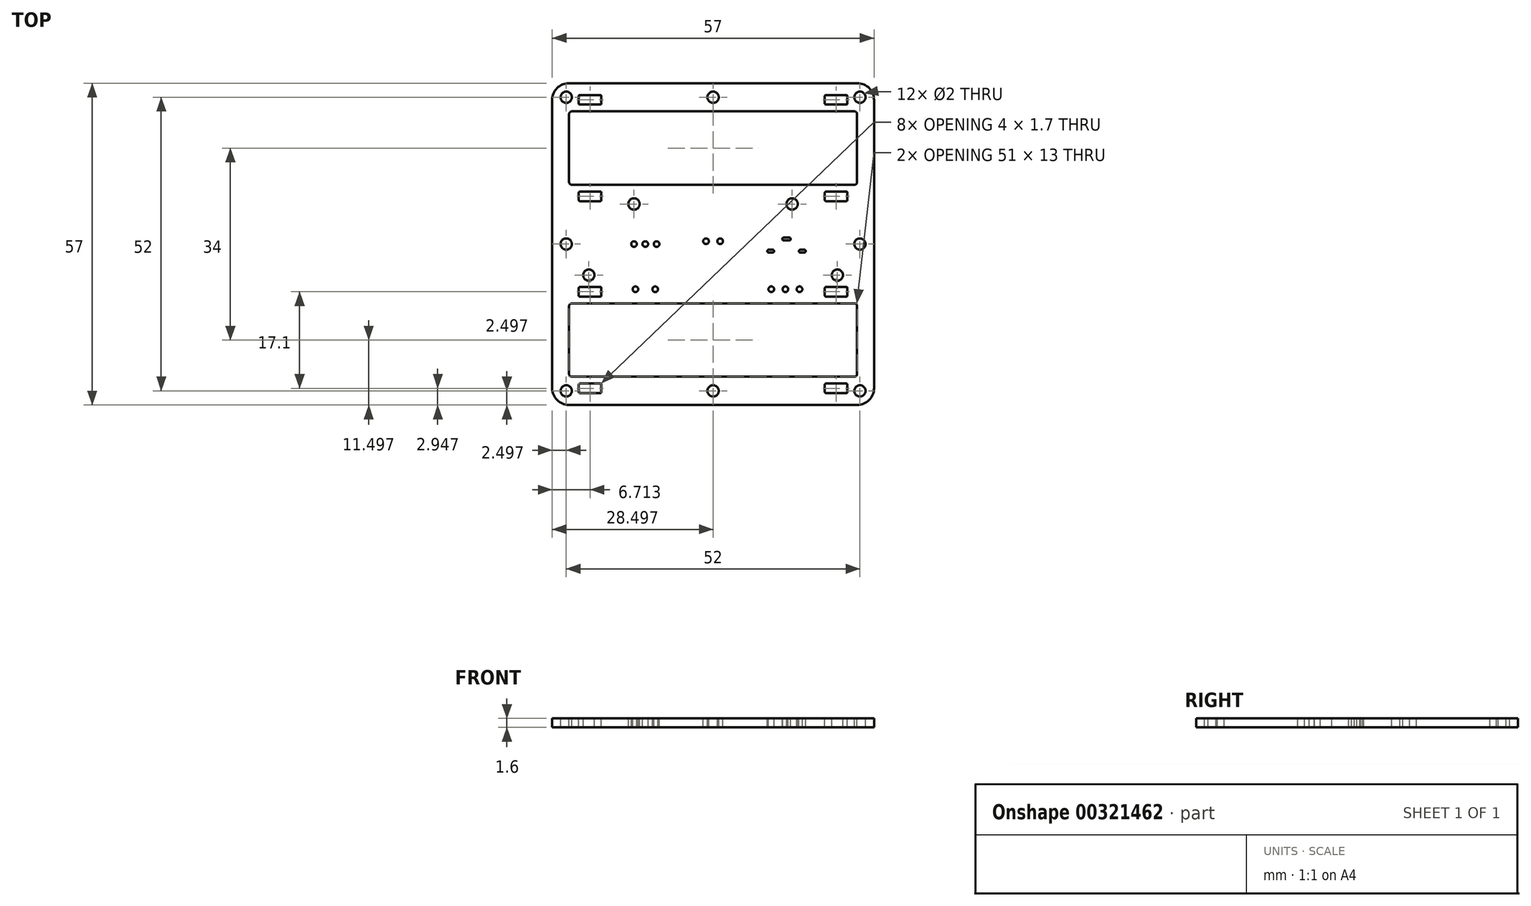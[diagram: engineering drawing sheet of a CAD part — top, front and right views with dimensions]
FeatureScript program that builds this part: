
annotation { "Feature Type Name" : "Feature", "Feature Type Description" : "" }
export const myFeature = defineFeature(function(context is Context, id is Id, definition is map)
    precondition{}
    {
        {
            var Q0;
            Q0=qCreatedBy(makeId("Top.planeOp"),FACE);
            var sketch = newSketch(context, id + "F0", { "sketchPlane" : qUnion([Q0])});
            skLineSegment(sketch, "E0.bottom", {"start": v(24.47, 58.7) * mm, "end": v(66.84, 58.7) * mm, "construction": true});
            skLineSegment(sketch, "E1.bottom", {"start": v(12.82, 58.7) * mm, "end": v(69.82, 58.7) * mm});
            skLineSegment(sketch, "E1.top", {"start": v(12.82, 1.7) * mm, "end": v(69.82, 1.7) * mm});
            skLineSegment(sketch, "E1.left", {"start": v(12.82, 58.7) * mm, "end": v(12.82, 1.7) * mm});
            skLineSegment(sketch, "E1.right", {"start": v(69.82, 58.7) * mm, "end": v(69.82, 1.7) * mm});
            skLineSegment(sketch, "E2", {"start": v(41.32, 58.7) * mm, "end": v(41.32, 1.7) * mm, "construction": true});
            skSolve(sketch);
        }
        {
            var Q0;
            Q0=qSketchRegion(id+"F0",true);
            extrude(context, id + "F1", {"entities" : qUnion([Q0]), "depth" : 1.6 * mm});
        }
        {
            var Q0;
            Q0=makeQuery(id+"F1.opExtrude","CAP_FACE",FACE,{"disambiguationData":[OSD([sQuery(id+"F0.wireOp",EDGE,"E1.bottom"),sQuery(id+"F0.wireOp",EDGE,"E1.top"),sQuery(id+"F0.wireOp",EDGE,"E1.left"),sQuery(id+"F0.wireOp",EDGE,"E1.right")])],"isStart":false});
            var sketch = newSketch(context, id + "F2", { "sketchPlane" : qUnion([Q0])});
            skCircle(sketch, "E3", {"center": v(27.32, 30.2) * mm, "radius": 0.5 * mm});
            skLineSegment(sketch, "E4", {"start": v(41.32, 22.32) * mm, "end": v(41.32, 29.29) * mm, "construction": true});
            skCircle(sketch, "E5.1.0.0", {"center": v(29.32, 30.2) * mm, "radius": 0.5 * mm});
            skLineSegment(sketch, "E5.direction1", {"start": v(27.32, 30.2) * mm, "end": v(29.32, 30.2) * mm, "construction": true});
            skCircle(sketch, "E6.0.2.0", {"center": v(31.32, 30.2) * mm, "radius": 0.5 * mm});
            skSolve(sketch);
        }
        {
            var Q0;
            Q0=makeQuery(id+"F1.opExtrude","CAP_FACE",FACE,{"disambiguationData":[OSD([sQuery(id+"F0.wireOp",EDGE,"E1.bottom"),sQuery(id+"F0.wireOp",EDGE,"E1.top"),sQuery(id+"F0.wireOp",EDGE,"E1.left"),sQuery(id+"F0.wireOp",EDGE,"E1.right")])],"isStart":false});
            var sketch = newSketch(context, id + "F3", { "sketchPlane" : qUnion([Q0])});
            skLineSegment(sketch, "E7", {"start": v(54.32, 14.1) * mm, "end": v(54.32, 27.42) * mm, "construction": true});
            skLineSegment(sketch, "E8", {"start": v(41.32, 6.29) * mm, "end": v(41.32, 24.04) * mm, "construction": true});
            skLineSegment(sketch, "E9", {"start": v(51.17, 28.95) * mm, "end": v(51.87, 28.95) * mm, "construction": true});
            skLineSegment(sketch, "E10", {"start": v(51.52, 23.97) * mm, "end": v(51.52, 28.95) * mm, "construction": true});
            skLineSegment(sketch, "E11", {"start": v(53.82, 31.1) * mm, "end": v(54.82, 31.1) * mm, "construction": true});
            skLineSegment(sketch, "E12", {"start": v(54.32, 31.1) * mm, "end": v(54.32, 19.92) * mm, "construction": true});
            skArc(sketch, "E13.0.startCap", {"start": v(53.82, 30.85) * mm, "mid": v(53.57, 31.1) * mm, "end": v(53.82, 31.35) * mm});
            skArc(sketch, "E13.0.endCap", {"start": v(54.82, 31.35) * mm, "mid": v(55.07, 31.1) * mm, "end": v(54.82, 30.85) * mm});
            skLineSegment(sketch, "E13.0.left", {"start": v(53.82, 31.35) * mm, "end": v(54.82, 31.35) * mm});
            skLineSegment(sketch, "E13.0.right", {"start": v(53.82, 30.85) * mm, "end": v(54.82, 30.85) * mm});
            skLineSegment(sketch, "E14", {"start": v(50.45, 30.1) * mm, "end": v(53.65, 30.1) * mm, "construction": true});
            skArc(sketch, "E15.0.startCap", {"start": v(51.87, 29.2) * mm, "mid": v(52.12, 28.95) * mm, "end": v(51.87, 28.7) * mm});
            skArc(sketch, "E15.0.endCap", {"start": v(51.17, 28.7) * mm, "mid": v(50.92, 28.95) * mm, "end": v(51.17, 29.2) * mm});
            skLineSegment(sketch, "E15.0.left", {"start": v(51.17, 28.7) * mm, "end": v(51.87, 28.7) * mm});
            skLineSegment(sketch, "E15.0.right", {"start": v(51.17, 29.2) * mm, "end": v(51.87, 29.2) * mm});
            skArc(sketch, "E16.MirrorCS", {"start": v(57.47, 28.7) * mm, "mid": v(57.72, 28.95) * mm, "end": v(57.47, 29.2) * mm});
            skLineSegment(sketch, "E17.MirrorCS", {"start": v(57.47, 28.7) * mm, "end": v(56.77, 28.7) * mm});
            skLineSegment(sketch, "E18.MirrorCS", {"start": v(57.47, 29.2) * mm, "end": v(56.77, 29.2) * mm});
            skArc(sketch, "E19.MirrorCS", {"start": v(56.77, 29.2) * mm, "mid": v(56.52, 28.95) * mm, "end": v(56.77, 28.7) * mm});
            skSolve(sketch);
        }
        {
            var Q0;
            Q0=makeQuery(id+"F1.opExtrude","CAP_FACE",FACE,{"disambiguationData":[OSD([sQuery(id+"F0.wireOp",EDGE,"E1.bottom"),sQuery(id+"F0.wireOp",EDGE,"E1.top"),sQuery(id+"F0.wireOp",EDGE,"E1.left"),sQuery(id+"F0.wireOp",EDGE,"E1.right")])],"isStart":false});
            var sketch = newSketch(context, id + "F4", { "sketchPlane" : qUnion([Q0])});
            skCircle(sketch, "E20", {"center": v(51.62, 22.2) * mm, "radius": 0.5 * mm});
            skCircle(sketch, "E21.1.0.0", {"center": v(56.62, 22.2) * mm, "radius": 0.5 * mm});
            skLineSegment(sketch, "E21.direction1", {"start": v(51.62, 22.2) * mm, "end": v(56.62, 22.2) * mm, "construction": true});
            skLineSegment(sketch, "E22", {"start": v(41.32, 6.29) * mm, "end": v(41.32, 17.65) * mm, "construction": true});
            skLineSegment(sketch, "E23", {"start": v(54.12, 22.2) * mm, "end": v(54.12, 23.7) * mm, "construction": true});
            skCircle(sketch, "E24", {"center": v(54.12, 22.2) * mm, "radius": 0.5 * mm});
            skSolve(sketch);
        }
        {
            var Q0;
            Q0=makeQuery(id+"F1.opExtrude","CAP_FACE",FACE,{"disambiguationData":[OSD([sQuery(id+"F0.wireOp",EDGE,"E1.bottom"),sQuery(id+"F0.wireOp",EDGE,"E1.top"),sQuery(id+"F0.wireOp",EDGE,"E1.left"),sQuery(id+"F0.wireOp",EDGE,"E1.right")])],"isStart":false});
            var sketch = newSketch(context, id + "F5", { "sketchPlane" : qUnion([Q0])});
            skCircle(sketch, "E25", {"center": v(40.07, 30.7) * mm, "radius": 0.5 * mm});
            skCircle(sketch, "E26.1.0.0", {"center": v(42.57, 30.7) * mm, "radius": 0.5 * mm});
            skLineSegment(sketch, "E26.direction1", {"start": v(40.07, 30.7) * mm, "end": v(42.57, 30.7) * mm, "construction": true});
            skLineSegment(sketch, "E27", {"start": v(41.32, 15.29) * mm, "end": v(41.32, 29.29) * mm, "construction": true});
            skLineSegment(sketch, "E28", {"start": v(41.32, 26.14) * mm, "end": v(41.32, 30.7) * mm, "construction": true});
            skSolve(sketch);
        }
        {
            var Q0;
            Q0=makeQuery(id+"F1.opExtrude","CAP_FACE",FACE,{"disambiguationData":[OSD([sQuery(id+"F0.wireOp",EDGE,"E1.bottom"),sQuery(id+"F0.wireOp",EDGE,"E1.top"),sQuery(id+"F0.wireOp",EDGE,"E1.left"),sQuery(id+"F0.wireOp",EDGE,"E1.right")])],"isStart":false});
            var sketch = newSketch(context, id + "F6", { "sketchPlane" : qUnion([Q0])});
            skCircle(sketch, "E29", {"center": v(27.57, 22.2) * mm, "radius": 0.5 * mm});
            skCircle(sketch, "E30.1.0.0", {"center": v(31.07, 22.2) * mm, "radius": 0.5 * mm});
            skLineSegment(sketch, "E30.direction1", {"start": v(27.57, 22.2) * mm, "end": v(31.07, 22.2) * mm, "construction": true});
            skLineSegment(sketch, "E31", {"start": v(29.32, 26.4) * mm, "end": v(29.32, 22.2) * mm, "construction": true});
            skSolve(sketch);
        }
        {
            var Q0;
            Q0=qSketchRegion(id+"F4",true);
            var Q1;
            Q1=qSketchRegion(id+"F5",true);
            var Q2;
            Q2=qSketchRegion(id+"F6",true);
            var Q3;
            Q3=qSketchRegion(id+"F3",true);
            var Q4;
            Q4=qSketchRegion(id+"F2",true);
            extrude(context, id + "F7", {"entities" : qUnion([Q0, Q1, Q2, Q3, Q4]), "operationType" : NewBodyOperationType.REMOVE, "oppositeDirection" : true, "depth" : 4 * mm});
        }
        {
            var Q0;
            Q0=makeQuery(id+"F1.opExtrude","SWEPT_EDGE",EDGE,{"disambiguationData":[OSD([sQuery(id+"F0.wireOp",EDGE,"E1.top"),sQuery(id+"F0.wireOp",EDGE,"E1.left")])]});
            var Q1;
            Q1=makeQuery(id+"F1.opExtrude","SWEPT_EDGE",EDGE,{"disambiguationData":[OSD([sQuery(id+"F0.wireOp",EDGE,"E1.top"),sQuery(id+"F0.wireOp",EDGE,"E1.right")])]});
            var Q2;
            Q2=makeQuery(id+"F1.opExtrude","SWEPT_EDGE",EDGE,{"disambiguationData":[OSD([sQuery(id+"F0.wireOp",EDGE,"E1.bottom"),sQuery(id+"F0.wireOp",EDGE,"E1.right")])]});
            var Q3;
            Q3=makeQuery(id+"F1.opExtrude","SWEPT_EDGE",EDGE,{"disambiguationData":[OSD([sQuery(id+"F0.wireOp",EDGE,"E1.bottom"),sQuery(id+"F0.wireOp",EDGE,"E1.left")])]});
            fillet(context, id + "F8", {"entities" : qUnion([Q0, Q1, Q2, Q3]), "radius" : 3 * mm, "tangentPropagation" : true, "allowEdgeOverflow" : false});
        }
        {
            var Q0;
            Q0=makeQuery(id+"F1.opExtrude","CAP_FACE",FACE,{"disambiguationData":[OSD([sQuery(id+"F0.wireOp",EDGE,"E1.bottom"),sQuery(id+"F0.wireOp",EDGE,"E1.top"),sQuery(id+"F0.wireOp",EDGE,"E1.left"),sQuery(id+"F0.wireOp",EDGE,"E1.right")])],"isStart":false});
            var sketch = newSketch(context, id + "F9", { "sketchPlane" : qUnion([Q0])});
            skLineSegment(sketch, "E32", {"start": v(41.32, 58.7) * mm, "end": v(41.32, 1.7) * mm, "construction": true});
            skLineSegment(sketch, "E33", {"start": v(12.82, 30.2) * mm, "end": v(69.82, 30.2) * mm, "construction": true});
            skCircle(sketch, "E34", {"center": v(63.32, 24.7) * mm, "radius": 1 * mm});
            skCircle(sketch, "E35.MirrorC", {"center": v(19.32, 24.7) * mm, "radius": 1 * mm});
            skCircle(sketch, "E36", {"center": v(55.32, 37.3) * mm, "radius": 1 * mm});
            skCircle(sketch, "E37.MirrorC", {"center": v(27.32, 37.3) * mm, "radius": 1 * mm});
            skCircle(sketch, "E38", {"center": v(15.32, 56.2) * mm, "radius": 1 * mm});
            skCircle(sketch, "E39.MirrorC", {"center": v(67.32, 56.2) * mm, "radius": 1 * mm});
            skCircle(sketch, "E40.MirrorC", {"center": v(15.32, 4.2) * mm, "radius": 1 * mm});
            skCircle(sketch, "E41.MirrorC", {"center": v(67.32, 4.2) * mm, "radius": 1 * mm});
            skCircle(sketch, "E42", {"center": v(41.32, 56.2) * mm, "radius": 1 * mm});
            skCircle(sketch, "E43.MirrorC", {"center": v(41.32, 4.2) * mm, "radius": 1 * mm});
            skCircle(sketch, "E44", {"center": v(15.32, 30.2) * mm, "radius": 1 * mm});
            skCircle(sketch, "E45", {"center": v(67.32, 30.2) * mm, "radius": 1 * mm});
            skSolve(sketch);
        }
        {
            var Q0;
            Q0=qSketchRegion(id+"F9",true);
            extrude(context, id + "F10", {"entities" : qUnion([Q0]), "operationType" : NewBodyOperationType.REMOVE, "oppositeDirection" : true, "depth" : 25 * mm});
        }
        {
            var Q0;
            Q0=makeQuery(id+"F1.opExtrude","CAP_FACE",FACE,{"disambiguationData":[OSD([sQuery(id+"F0.wireOp",EDGE,"E1.bottom"),sQuery(id+"F0.wireOp",EDGE,"E1.top"),sQuery(id+"F0.wireOp",EDGE,"E1.left"),sQuery(id+"F0.wireOp",EDGE,"E1.right")])],"isStart":false});
            var sketch = newSketch(context, id + "F11", { "sketchPlane" : qUnion([Q0])});
            skLineSegment(sketch, "E46", {"start": v(41.32, 58.7) * mm, "end": v(41.32, 1.7) * mm, "construction": true});
            skLineSegment(sketch, "E47.bottom", {"start": v(66.32, 19.7) * mm, "end": v(16.32, 19.7) * mm});
            skLineSegment(sketch, "E47.top", {"start": v(66.32, 6.7) * mm, "end": v(16.32, 6.7) * mm});
            skLineSegment(sketch, "E47.left", {"start": v(66.82, 19.2) * mm, "end": v(66.82, 7.2) * mm});
            skLineSegment(sketch, "E47.right", {"start": v(15.82, 19.2) * mm, "end": v(15.82, 7.2) * mm});
            skPoint(sketch, "E47.middle", {"position": v(41.32, 13.2) * mm});
            skLineSegment(sketch, "E48", {"start": v(41.32, 30.2) * mm, "end": v(-6.1, 30.2) * mm, "construction": true});
            skPoint(sketch, "E49.visualSharp", {"position": v(15.82, 6.7) * mm});
            skArc(sketch, "E49.filletArc", {"start": v(15.82, 7.2) * mm, "mid": v(15.96, 6.84) * mm, "end": v(16.32, 6.7) * mm});
            skPoint(sketch, "E50.visualSharp", {"position": v(15.82, 19.7) * mm});
            skArc(sketch, "E50.filletArc", {"start": v(16.32, 19.7) * mm, "mid": v(15.96, 19.55) * mm, "end": v(15.82, 19.2) * mm});
            skPoint(sketch, "E51.visualSharp", {"position": v(66.82, 19.7) * mm});
            skArc(sketch, "E51.filletArc", {"start": v(66.82, 19.2) * mm, "mid": v(66.67, 19.55) * mm, "end": v(66.32, 19.7) * mm});
            skPoint(sketch, "E52.visualSharp", {"position": v(66.82, 6.7) * mm});
            skArc(sketch, "E52.filletArc", {"start": v(66.32, 6.7) * mm, "mid": v(66.67, 6.84) * mm, "end": v(66.82, 7.2) * mm});
            skArc(sketch, "E53.MirrorCS", {"start": v(15.82, 53.2) * mm, "mid": v(15.96, 53.55) * mm, "end": v(16.32, 53.7) * mm});
            skArc(sketch, "E54.MirrorCS", {"start": v(16.32, 40.7) * mm, "mid": v(15.96, 40.84) * mm, "end": v(15.82, 41.2) * mm});
            skArc(sketch, "E55.MirrorCS", {"start": v(66.82, 41.2) * mm, "mid": v(66.67, 40.84) * mm, "end": v(66.32, 40.7) * mm});
            skArc(sketch, "E56.MirrorCS", {"start": v(66.32, 53.7) * mm, "mid": v(66.67, 53.55) * mm, "end": v(66.82, 53.2) * mm});
            skLineSegment(sketch, "E57.MirrorCS", {"start": v(15.82, 41.2) * mm, "end": v(15.82, 53.2) * mm});
            skLineSegment(sketch, "E58.MirrorCS", {"start": v(66.32, 40.7) * mm, "end": v(16.32, 40.7) * mm});
            skLineSegment(sketch, "E59.MirrorCS", {"start": v(66.82, 41.2) * mm, "end": v(66.82, 53.2) * mm});
            skLineSegment(sketch, "E60.MirrorCS", {"start": v(66.32, 53.7) * mm, "end": v(16.32, 53.7) * mm});
            skPoint(sketch, "E61.MirrorP", {"position": v(66.82, 53.7) * mm});
            skPoint(sketch, "E62.MirrorP", {"position": v(15.82, 53.7) * mm});
            skPoint(sketch, "E63.MirrorP", {"position": v(41.32, 47.2) * mm});
            skPoint(sketch, "E64.MirrorP", {"position": v(66.82, 40.7) * mm});
            skPoint(sketch, "E65.MirrorP", {"position": v(15.82, 40.7) * mm});
            skSolve(sketch);
        }
        {
            var Q0;
            Q0=qSketchRegion(id+"F11",true);
            extrude(context, id + "F12", {"entities" : qUnion([Q0]), "operationType" : NewBodyOperationType.REMOVE, "oppositeDirection" : true, "depth" : 5 * mm});
        }
        {
            var Q0;
            Q0=makeQuery(id+"F1.opExtrude","CAP_FACE",FACE,{"disambiguationData":[OSD([sQuery(id+"F0.wireOp",EDGE,"E1.bottom"),sQuery(id+"F0.wireOp",EDGE,"E1.top"),sQuery(id+"F0.wireOp",EDGE,"E1.left"),sQuery(id+"F0.wireOp",EDGE,"E1.right")])],"isStart":false});
            var sketch = newSketch(context, id + "F13", { "sketchPlane" : qUnion([Q0])});
            skLineSegment(sketch, "E66.bottom", {"start": v(17.53, 5.5) * mm, "end": v(21.53, 5.5) * mm});
            skLineSegment(sketch, "E66.top", {"start": v(17.53, 3.8) * mm, "end": v(21.53, 3.8) * mm});
            skLineSegment(sketch, "E66.left", {"start": v(17.53, 5.5) * mm, "end": v(17.53, 3.8) * mm});
            skLineSegment(sketch, "E66.right", {"start": v(21.53, 5.5) * mm, "end": v(21.53, 3.8) * mm});
            skLineSegment(sketch, "E67.MirrorCS", {"start": v(65.1, 5.5) * mm, "end": v(65.1, 3.8) * mm});
            skLineSegment(sketch, "E68.MirrorCS", {"start": v(61.1, 5.5) * mm, "end": v(61.1, 3.8) * mm});
            skLineSegment(sketch, "E69.MirrorCS", {"start": v(65.1, 3.8) * mm, "end": v(61.1, 3.8) * mm});
            skLineSegment(sketch, "E70.MirrorCS", {"start": v(65.1, 5.5) * mm, "end": v(61.1, 5.5) * mm});
            skLineSegment(sketch, "E71", {"start": v(12.82, 30.2) * mm, "end": v(83.5, 30.2) * mm, "construction": true});
            skLineSegment(sketch, "E72", {"start": v(15.82, 13.2) * mm, "end": v(-2.11, 13.2) * mm, "construction": true});
            skPoint(sketch, "E72.endSnap0", {"position": v(15.82, 13.2) * mm});
            skLineSegment(sketch, "E73.MirrorCS", {"start": v(61.1, 20.9) * mm, "end": v(61.1, 22.6) * mm});
            skLineSegment(sketch, "E74.MirrorCS", {"start": v(65.1, 20.9) * mm, "end": v(65.1, 22.6) * mm});
            skLineSegment(sketch, "E75.MirrorCS", {"start": v(21.53, 20.9) * mm, "end": v(21.53, 22.6) * mm});
            skLineSegment(sketch, "E76.MirrorCS", {"start": v(17.53, 20.9) * mm, "end": v(17.53, 22.6) * mm});
            skLineSegment(sketch, "E77.MirrorCS", {"start": v(65.1, 20.9) * mm, "end": v(61.1, 20.9) * mm});
            skLineSegment(sketch, "E78.MirrorCS", {"start": v(65.1, 22.6) * mm, "end": v(61.1, 22.6) * mm});
            skLineSegment(sketch, "E79.MirrorCS", {"start": v(17.53, 22.6) * mm, "end": v(21.53, 22.6) * mm});
            skLineSegment(sketch, "E80.MirrorCS", {"start": v(17.53, 20.9) * mm, "end": v(21.53, 20.9) * mm});
            skLineSegment(sketch, "E81.MirrorCS", {"start": v(17.53, 39.5) * mm, "end": v(17.53, 37.8) * mm});
            skLineSegment(sketch, "E82.MirrorCS", {"start": v(17.53, 54.9) * mm, "end": v(17.53, 56.6) * mm});
            skLineSegment(sketch, "E83.MirrorCS", {"start": v(61.1, 39.5) * mm, "end": v(61.1, 37.8) * mm});
            skLineSegment(sketch, "E84.MirrorCS", {"start": v(21.53, 54.9) * mm, "end": v(21.53, 56.6) * mm});
            skLineSegment(sketch, "E85.MirrorCS", {"start": v(65.1, 54.9) * mm, "end": v(65.1, 56.6) * mm});
            skLineSegment(sketch, "E86.MirrorCS", {"start": v(21.53, 39.5) * mm, "end": v(21.53, 37.8) * mm});
            skLineSegment(sketch, "E87.MirrorCS", {"start": v(61.1, 54.9) * mm, "end": v(61.1, 56.6) * mm});
            skLineSegment(sketch, "E88.MirrorCS", {"start": v(65.1, 39.5) * mm, "end": v(65.1, 37.8) * mm});
            skLineSegment(sketch, "E89.MirrorCS", {"start": v(17.53, 56.6) * mm, "end": v(21.53, 56.6) * mm});
            skLineSegment(sketch, "E90.MirrorCS", {"start": v(65.1, 39.5) * mm, "end": v(61.1, 39.5) * mm});
            skLineSegment(sketch, "E91.MirrorCS", {"start": v(65.1, 37.8) * mm, "end": v(61.1, 37.8) * mm});
            skLineSegment(sketch, "E92.MirrorCS", {"start": v(17.53, 39.5) * mm, "end": v(21.53, 39.5) * mm});
            skLineSegment(sketch, "E93.MirrorCS", {"start": v(17.53, 54.9) * mm, "end": v(21.53, 54.9) * mm});
            skLineSegment(sketch, "E94.MirrorCS", {"start": v(65.1, 56.6) * mm, "end": v(61.1, 56.6) * mm});
            skPoint(sketch, "E95.MirrorP", {"position": v(15.82, 47.2) * mm});
            skLineSegment(sketch, "E96.MirrorCS", {"start": v(65.1, 54.9) * mm, "end": v(61.1, 54.9) * mm});
            skLineSegment(sketch, "E97.MirrorCS", {"start": v(17.53, 37.8) * mm, "end": v(21.53, 37.8) * mm});
            skSolve(sketch);
        }
        {
            var Q0;
            Q0=qSketchRegion(id+"F13",true);
            extrude(context, id + "F14", {"entities" : qUnion([Q0]), "operationType" : NewBodyOperationType.REMOVE, "oppositeDirection" : true, "depth" : 25 * mm});
        }
        {
            var Q0;
            Q0=makeQuery(id+"F14.boolean.opBoolean","COPY",EDGE,{"derivedFrom":makeQuery(id+"F14.opExtrude","SWEPT_EDGE",EDGE,{"disambiguationData":[OSD([sQuery(id+"F13.wireOp",EDGE,"E82.MirrorCS"),sQuery(id+"F13.wireOp",EDGE,"E89.MirrorCS")])]})});
            var Q1;
            Q1=makeQuery(id+"F14.boolean.opBoolean","COPY",EDGE,{"derivedFrom":makeQuery(id+"F14.opExtrude","SWEPT_EDGE",EDGE,{"disambiguationData":[OSD([sQuery(id+"F13.wireOp",EDGE,"E82.MirrorCS"),sQuery(id+"F13.wireOp",EDGE,"E93.MirrorCS")])]})});
            var Q2;
            Q2=makeQuery(id+"F14.boolean.opBoolean","COPY",EDGE,{"derivedFrom":makeQuery(id+"F14.opExtrude","SWEPT_EDGE",EDGE,{"disambiguationData":[OSD([sQuery(id+"F13.wireOp",EDGE,"E84.MirrorCS"),sQuery(id+"F13.wireOp",EDGE,"E93.MirrorCS")])]})});
            var Q3;
            Q3=makeQuery(id+"F14.boolean.opBoolean","COPY",EDGE,{"derivedFrom":makeQuery(id+"F14.opExtrude","SWEPT_EDGE",EDGE,{"disambiguationData":[OSD([sQuery(id+"F13.wireOp",EDGE,"E84.MirrorCS"),sQuery(id+"F13.wireOp",EDGE,"E89.MirrorCS")])]})});
            var Q4;
            Q4=makeQuery(id+"F14.boolean.opBoolean","COPY",EDGE,{"derivedFrom":makeQuery(id+"F14.opExtrude","SWEPT_EDGE",EDGE,{"disambiguationData":[OSD([sQuery(id+"F13.wireOp",EDGE,"E86.MirrorCS"),sQuery(id+"F13.wireOp",EDGE,"E92.MirrorCS")])]})});
            var Q5;
            Q5=makeQuery(id+"F14.boolean.opBoolean","COPY",EDGE,{"derivedFrom":makeQuery(id+"F14.opExtrude","SWEPT_EDGE",EDGE,{"disambiguationData":[OSD([sQuery(id+"F13.wireOp",EDGE,"E81.MirrorCS"),sQuery(id+"F13.wireOp",EDGE,"E92.MirrorCS")])]})});
            var Q6;
            Q6=makeQuery(id+"F14.boolean.opBoolean","COPY",EDGE,{"derivedFrom":makeQuery(id+"F14.opExtrude","SWEPT_EDGE",EDGE,{"disambiguationData":[OSD([sQuery(id+"F13.wireOp",EDGE,"E81.MirrorCS"),sQuery(id+"F13.wireOp",EDGE,"E97.MirrorCS")])]})});
            var Q7;
            Q7=makeQuery(id+"F14.boolean.opBoolean","COPY",EDGE,{"derivedFrom":makeQuery(id+"F14.opExtrude","SWEPT_EDGE",EDGE,{"disambiguationData":[OSD([sQuery(id+"F13.wireOp",EDGE,"E86.MirrorCS"),sQuery(id+"F13.wireOp",EDGE,"E97.MirrorCS")])]})});
            var Q8;
            Q8=makeQuery(id+"F14.boolean.opBoolean","COPY",EDGE,{"derivedFrom":makeQuery(id+"F14.opExtrude","SWEPT_EDGE",EDGE,{"disambiguationData":[OSD([sQuery(id+"F13.wireOp",EDGE,"E85.MirrorCS"),sQuery(id+"F13.wireOp",EDGE,"E96.MirrorCS")])]})});
            var Q9;
            Q9=makeQuery(id+"F14.boolean.opBoolean","COPY",EDGE,{"derivedFrom":makeQuery(id+"F14.opExtrude","SWEPT_EDGE",EDGE,{"disambiguationData":[OSD([sQuery(id+"F13.wireOp",EDGE,"E85.MirrorCS"),sQuery(id+"F13.wireOp",EDGE,"E94.MirrorCS")])]})});
            var Q10;
            Q10=makeQuery(id+"F14.boolean.opBoolean","COPY",EDGE,{"derivedFrom":makeQuery(id+"F14.opExtrude","SWEPT_EDGE",EDGE,{"disambiguationData":[OSD([sQuery(id+"F13.wireOp",EDGE,"E87.MirrorCS"),sQuery(id+"F13.wireOp",EDGE,"E94.MirrorCS")])]})});
            var Q11;
            Q11=makeQuery(id+"F14.boolean.opBoolean","COPY",EDGE,{"derivedFrom":makeQuery(id+"F14.opExtrude","SWEPT_EDGE",EDGE,{"disambiguationData":[OSD([sQuery(id+"F13.wireOp",EDGE,"E87.MirrorCS"),sQuery(id+"F13.wireOp",EDGE,"E96.MirrorCS")])]})});
            var Q12;
            Q12=makeQuery(id+"F14.boolean.opBoolean","COPY",EDGE,{"derivedFrom":makeQuery(id+"F14.opExtrude","SWEPT_EDGE",EDGE,{"disambiguationData":[OSD([sQuery(id+"F13.wireOp",EDGE,"E83.MirrorCS"),sQuery(id+"F13.wireOp",EDGE,"E91.MirrorCS")])]})});
            var Q13;
            Q13=makeQuery(id+"F14.boolean.opBoolean","COPY",EDGE,{"derivedFrom":makeQuery(id+"F14.opExtrude","SWEPT_EDGE",EDGE,{"disambiguationData":[OSD([sQuery(id+"F13.wireOp",EDGE,"E83.MirrorCS"),sQuery(id+"F13.wireOp",EDGE,"E90.MirrorCS")])]})});
            var Q14;
            Q14=makeQuery(id+"F14.boolean.opBoolean","COPY",EDGE,{"derivedFrom":makeQuery(id+"F14.opExtrude","SWEPT_EDGE",EDGE,{"disambiguationData":[OSD([sQuery(id+"F13.wireOp",EDGE,"E88.MirrorCS"),sQuery(id+"F13.wireOp",EDGE,"E90.MirrorCS")])]})});
            var Q15;
            Q15=makeQuery(id+"F14.boolean.opBoolean","COPY",EDGE,{"derivedFrom":makeQuery(id+"F14.opExtrude","SWEPT_EDGE",EDGE,{"disambiguationData":[OSD([sQuery(id+"F13.wireOp",EDGE,"E88.MirrorCS"),sQuery(id+"F13.wireOp",EDGE,"E91.MirrorCS")])]})});
            var Q16;
            Q16=makeQuery(id+"F14.boolean.opBoolean","COPY",EDGE,{"derivedFrom":makeQuery(id+"F14.opExtrude","SWEPT_EDGE",EDGE,{"disambiguationData":[OSD([sQuery(id+"F13.wireOp",EDGE,"E75.MirrorCS"),sQuery(id+"F13.wireOp",EDGE,"E80.MirrorCS")])]})});
            var Q17;
            Q17=makeQuery(id+"F14.boolean.opBoolean","COPY",EDGE,{"derivedFrom":makeQuery(id+"F14.opExtrude","SWEPT_EDGE",EDGE,{"disambiguationData":[OSD([sQuery(id+"F13.wireOp",EDGE,"E75.MirrorCS"),sQuery(id+"F13.wireOp",EDGE,"E79.MirrorCS")])]})});
            var Q18;
            Q18=makeQuery(id+"F14.boolean.opBoolean","COPY",EDGE,{"derivedFrom":makeQuery(id+"F14.opExtrude","SWEPT_EDGE",EDGE,{"disambiguationData":[OSD([sQuery(id+"F13.wireOp",EDGE,"E76.MirrorCS"),sQuery(id+"F13.wireOp",EDGE,"E79.MirrorCS")])]})});
            var Q19;
            Q19=makeQuery(id+"F14.boolean.opBoolean","COPY",EDGE,{"derivedFrom":makeQuery(id+"F14.opExtrude","SWEPT_EDGE",EDGE,{"disambiguationData":[OSD([sQuery(id+"F13.wireOp",EDGE,"E76.MirrorCS"),sQuery(id+"F13.wireOp",EDGE,"E80.MirrorCS")])]})});
            var Q20;
            Q20=makeQuery(id+"F14.boolean.opBoolean","COPY",EDGE,{"derivedFrom":makeQuery(id+"F14.opExtrude","SWEPT_EDGE",EDGE,{"disambiguationData":[OSD([sQuery(id+"F13.wireOp",EDGE,"E73.MirrorCS"),sQuery(id+"F13.wireOp",EDGE,"E77.MirrorCS")])]})});
            var Q21;
            Q21=makeQuery(id+"F14.boolean.opBoolean","COPY",EDGE,{"derivedFrom":makeQuery(id+"F14.opExtrude","SWEPT_EDGE",EDGE,{"disambiguationData":[OSD([sQuery(id+"F13.wireOp",EDGE,"E73.MirrorCS"),sQuery(id+"F13.wireOp",EDGE,"E78.MirrorCS")])]})});
            var Q22;
            Q22=makeQuery(id+"F14.boolean.opBoolean","COPY",EDGE,{"derivedFrom":makeQuery(id+"F14.opExtrude","SWEPT_EDGE",EDGE,{"disambiguationData":[OSD([sQuery(id+"F13.wireOp",EDGE,"E74.MirrorCS"),sQuery(id+"F13.wireOp",EDGE,"E78.MirrorCS")])]})});
            var Q23;
            Q23=makeQuery(id+"F14.boolean.opBoolean","COPY",EDGE,{"derivedFrom":makeQuery(id+"F14.opExtrude","SWEPT_EDGE",EDGE,{"disambiguationData":[OSD([sQuery(id+"F13.wireOp",EDGE,"E74.MirrorCS"),sQuery(id+"F13.wireOp",EDGE,"E77.MirrorCS")])]})});
            var Q24;
            Q24=makeQuery(id+"F14.boolean.opBoolean","COPY",EDGE,{"derivedFrom":makeQuery(id+"F14.opExtrude","SWEPT_EDGE",EDGE,{"disambiguationData":[OSD([sQuery(id+"F13.wireOp",EDGE,"E67.MirrorCS"),sQuery(id+"F13.wireOp",EDGE,"E69.MirrorCS")])]})});
            var Q25;
            Q25=makeQuery(id+"F14.boolean.opBoolean","COPY",EDGE,{"derivedFrom":makeQuery(id+"F14.opExtrude","SWEPT_EDGE",EDGE,{"disambiguationData":[OSD([sQuery(id+"F13.wireOp",EDGE,"E67.MirrorCS"),sQuery(id+"F13.wireOp",EDGE,"E70.MirrorCS")])]})});
            var Q26;
            Q26=makeQuery(id+"F14.boolean.opBoolean","COPY",EDGE,{"derivedFrom":makeQuery(id+"F14.opExtrude","SWEPT_EDGE",EDGE,{"disambiguationData":[OSD([sQuery(id+"F13.wireOp",EDGE,"E68.MirrorCS"),sQuery(id+"F13.wireOp",EDGE,"E70.MirrorCS")])]})});
            var Q27;
            Q27=makeQuery(id+"F14.boolean.opBoolean","COPY",EDGE,{"derivedFrom":makeQuery(id+"F14.opExtrude","SWEPT_EDGE",EDGE,{"disambiguationData":[OSD([sQuery(id+"F13.wireOp",EDGE,"E68.MirrorCS"),sQuery(id+"F13.wireOp",EDGE,"E69.MirrorCS")])]})});
            var Q28;
            Q28=makeQuery(id+"F14.boolean.opBoolean","COPY",EDGE,{"derivedFrom":makeQuery(id+"F14.opExtrude","SWEPT_EDGE",EDGE,{"disambiguationData":[OSD([sQuery(id+"F13.wireOp",EDGE,"E66.top"),sQuery(id+"F13.wireOp",EDGE,"E66.left")])]})});
            var Q29;
            Q29=makeQuery(id+"F14.boolean.opBoolean","COPY",EDGE,{"derivedFrom":makeQuery(id+"F14.opExtrude","SWEPT_EDGE",EDGE,{"disambiguationData":[OSD([sQuery(id+"F13.wireOp",EDGE,"E66.top"),sQuery(id+"F13.wireOp",EDGE,"E66.right")])]})});
            var Q30;
            Q30=makeQuery(id+"F14.boolean.opBoolean","COPY",EDGE,{"derivedFrom":makeQuery(id+"F14.opExtrude","SWEPT_EDGE",EDGE,{"disambiguationData":[OSD([sQuery(id+"F13.wireOp",EDGE,"E66.bottom"),sQuery(id+"F13.wireOp",EDGE,"E66.right")])]})});
            var Q31;
            Q31=makeQuery(id+"F14.boolean.opBoolean","COPY",EDGE,{"derivedFrom":makeQuery(id+"F14.opExtrude","SWEPT_EDGE",EDGE,{"disambiguationData":[OSD([sQuery(id+"F13.wireOp",EDGE,"E66.bottom"),sQuery(id+"F13.wireOp",EDGE,"E66.left")])]})});
            fillet(context, id + "F15", {"entities" : qUnion([Q0, Q1, Q2, Q3, Q4, Q5, Q6, Q7, Q8, Q9, Q10, Q11, Q12, Q13, Q14, Q15, Q16, Q17, Q18, Q19, Q20, Q21, Q22, Q23, Q24, Q25, Q26, Q27, Q28, Q29, Q30, Q31]), "radius" : .2 * mm, "tangentPropagation" : true, "allowEdgeOverflow" : false});
        }
    });
